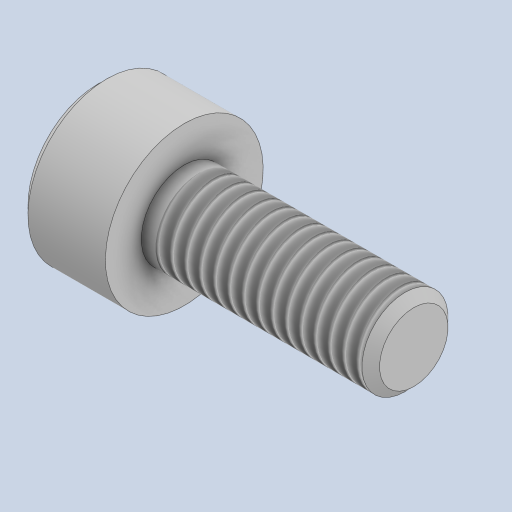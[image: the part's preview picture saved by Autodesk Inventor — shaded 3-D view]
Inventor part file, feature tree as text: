
AUTODESK INVENTOR PART (.ipt)
format: ipt  version: 2023 (Build 270158000, 158)  size: 206,336 bytes
history: native  units: mm
features: other x14, sketch x3, revolve x1, thread x1, hole x1, extrude x1
ambient origin geometry x8: Origin, YZ Plane, XZ Plane, XY Plane, X Axis, Y Axis, Z Axis, Center Point
bodies: Solid1 (feature_tree)
feature tree (21):
  revolve  "Revolution1"  [1 undecoded]
  thread  "Thread1"  [1 undecoded]
  hole  "Hole1"  [1 undecoded]
  extrude  "Extrusion1"  [1 undecoded]
  other  "bolt_XY"
  other  "bolt_YZ"
  other  "bolt_ZX"
  other  "bolt_X"
  other  "bolt_Y"
  other  "bolt_Z"
  other  "bolt_Center"
  other  "nut_XY"
  other  "nut_YZ"
  other  "nut_ZX"
  other  "nut_X"
  other  "nut_Y"
  other  "nut_Z"
  other  "nut_Center"
  sketch  "Sketch_1"  dims[d0=360.0deg d1=7.1935mm d2=0.0mm]
  sketch  "Sketch2"  dims[d3=2.5mm d4=6.0mm d5=4.0mm d6=2.0mm d7=90.0deg d8=1.3mm d9=120.0deg d10=1.3mm d11=0.0mm]
  sketch  "Sketch_3"  dims[d12=0.0mm d13=0.0mm]
note: 4 required parameter values undecoded (feature->parameter linkage not recoverable at this tier; creation-order binding heuristic only, values carry confidence <= 0.55)